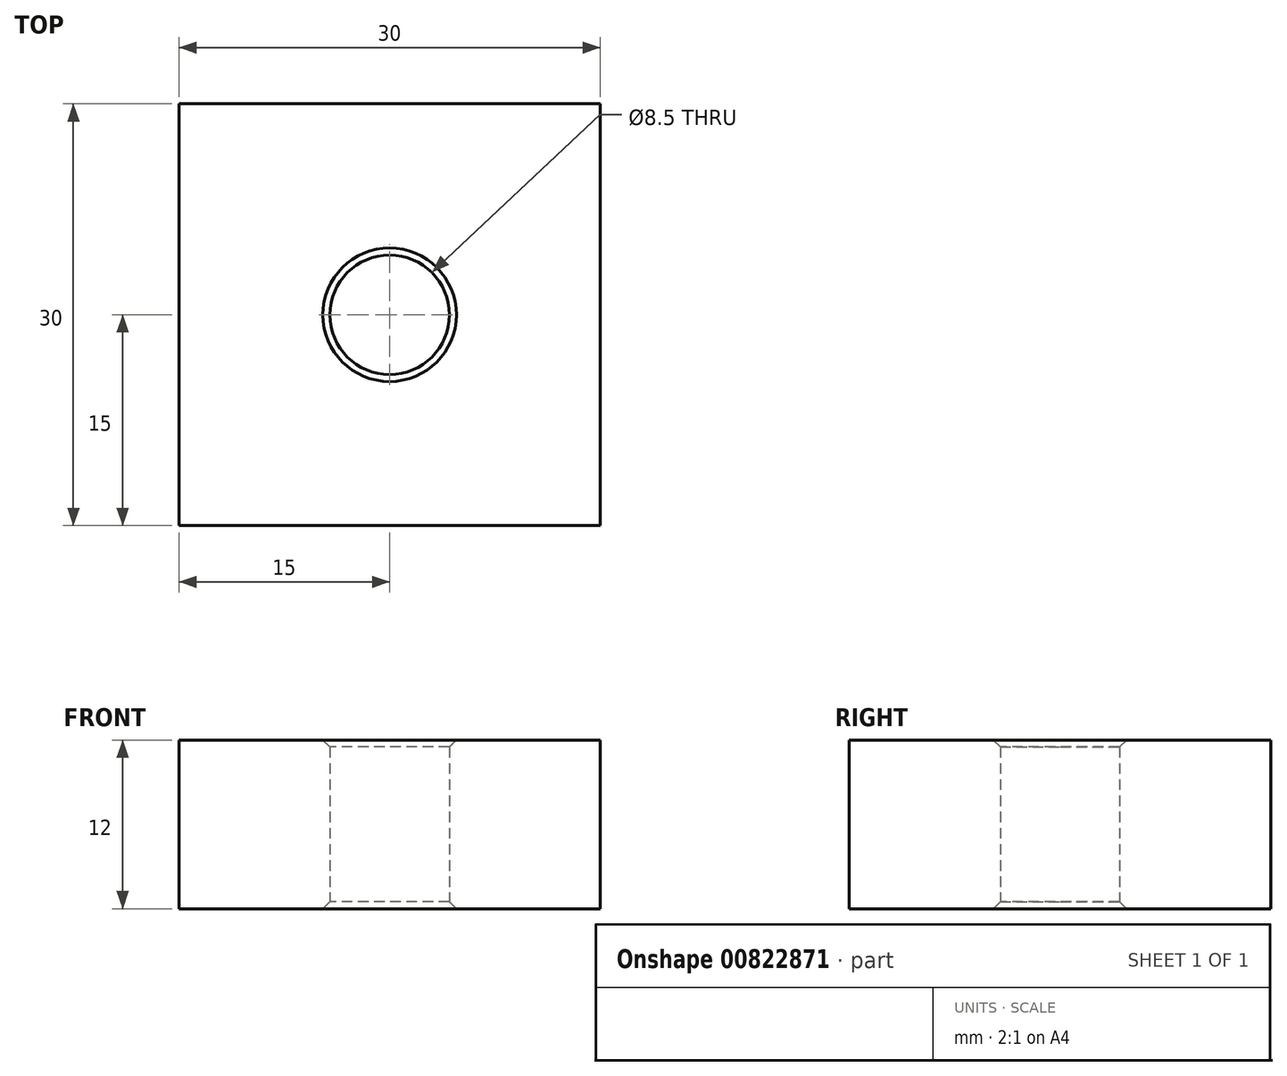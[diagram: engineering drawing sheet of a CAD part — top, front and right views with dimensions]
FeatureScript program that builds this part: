
annotation { "Feature Type Name" : "Feature", "Feature Type Description" : "" }
export const myFeature = defineFeature(function(context is Context, id is Id, definition is map)
    precondition{}
    {
        {
            var Q0;
            Q0=qCreatedBy(makeId("Top.planeOp"),FACE);
            var sketch = newSketch(context, id + "F0", { "sketchPlane" : qUnion([Q0])});
            skLineSegment(sketch, "E0.bottom", {"start": v(-15, -15) * mm, "end": v(15, -15) * mm});
            skLineSegment(sketch, "E0.top", {"start": v(-15, 15) * mm, "end": v(15, 15) * mm});
            skLineSegment(sketch, "E0.left", {"start": v(-15, -15) * mm, "end": v(-15, 15) * mm});
            skLineSegment(sketch, "E0.right", {"start": v(15, -15) * mm, "end": v(15, 15) * mm});
            skPoint(sketch, "E0.middle", {"position": v(0, 0) * mm});
            skCircle(sketch, "E1", {"center": v(0, 0) * mm, "radius": 4.25 * mm});
            skSolve(sketch);
        }
        {
            var Q0;
            Q0 = qSketchRegion(id + "F0", true);
            extrude(context, id + "F1", {"entities" : qUnion([Q0]), "depth" : 12 * mm, "offsetDistance" : 25 * mm});
        }
        {
            var Q0;
            Q0=makeQuery(id+"F1.opExtrude","SWEPT_FACE",FACE,{"disambiguationData":[OSD([sQuery(id+"F0.wireOp",EDGE,"E1")])]});
            chamfer(context, id + "F2", {"entities" : qUnion([Q0]), "width" : 0.5 * mm, "tangentPropagation" : true});
        }
    });
